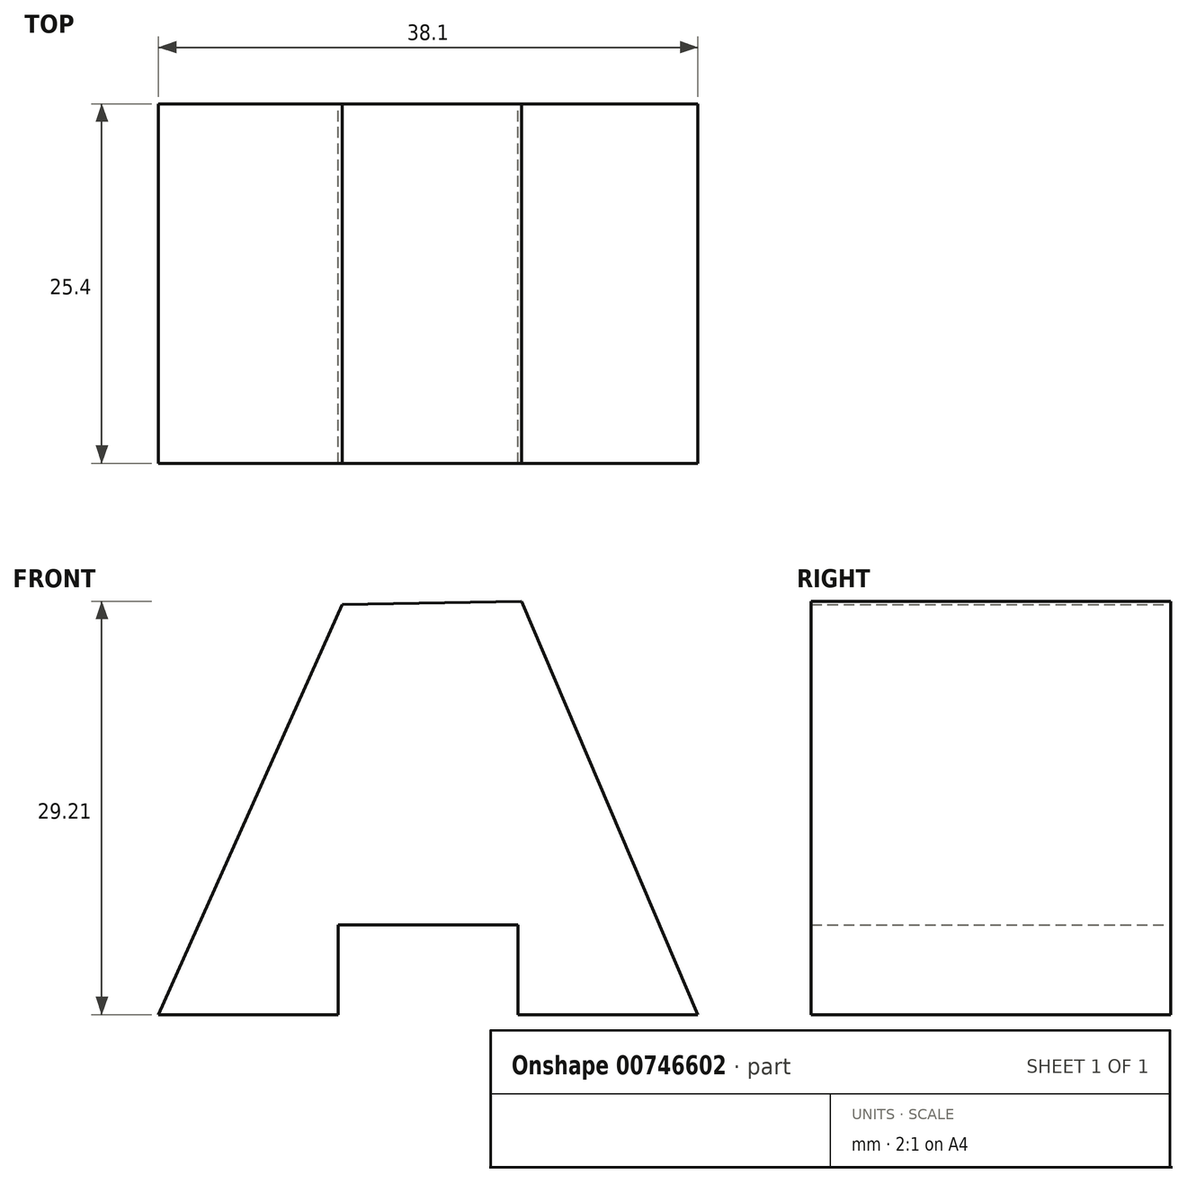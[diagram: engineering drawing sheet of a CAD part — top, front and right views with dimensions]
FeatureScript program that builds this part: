
annotation { "Feature Type Name" : "Feature", "Feature Type Description" : "" }
export const myFeature = defineFeature(function(context is Context, id is Id, definition is map)
    precondition{}
    {
        {
            var Q0;
            Q0=qCreatedBy(makeId("Front.planeOp"),FACE);
            var sketch = newSketch(context, id + "F0", { "sketchPlane" : qUnion([Q0])});
            skLineSegment(sketch, "E0", {"start": v(0, 0) * mm, "end": v(12.96, 28.98) * mm});
            skLineSegment(sketch, "E1", {"start": v(25.66, 29.21) * mm, "end": v(38.1, 0) * mm});
            skLineSegment(sketch, "E2", {"start": v(38.1, 0) * mm, "end": v(25.4, 0) * mm});
            skLineSegment(sketch, "E3", {"start": v(25.4, 0) * mm, "end": v(25.4, 6.35) * mm});
            skLineSegment(sketch, "E4", {"start": v(25.4, 6.35) * mm, "end": v(12.7, 6.35) * mm});
            skLineSegment(sketch, "E5", {"start": v(12.7, 6.35) * mm, "end": v(12.7, 0) * mm});
            skLineSegment(sketch, "E6", {"start": v(12.7, 0) * mm, "end": v(0, 0) * mm});
            skLineSegment(sketch, "E7", {"start": v(12.96, 28.98) * mm, "end": v(25.66, 29.21) * mm});
            skSolve(sketch);
        }
        {
            var Q0;
            Q0=makeQuery(id+"F0.imprint","IMPRINT",FACE,{"disambiguationData":[TD([[makeQuery(id+"F0.imprint","IMPRINT",EDGE,{"derivedFrom":sQuery(id+"F0.wireOp",EDGE,"E0")}),-1.0]])]});
            extrude(context, id + "F1", {"entities" : qUnion([Q0]), "depth" : 25.4 * mm, "offsetDistance" : 25.4 * mm});
        }
    });
